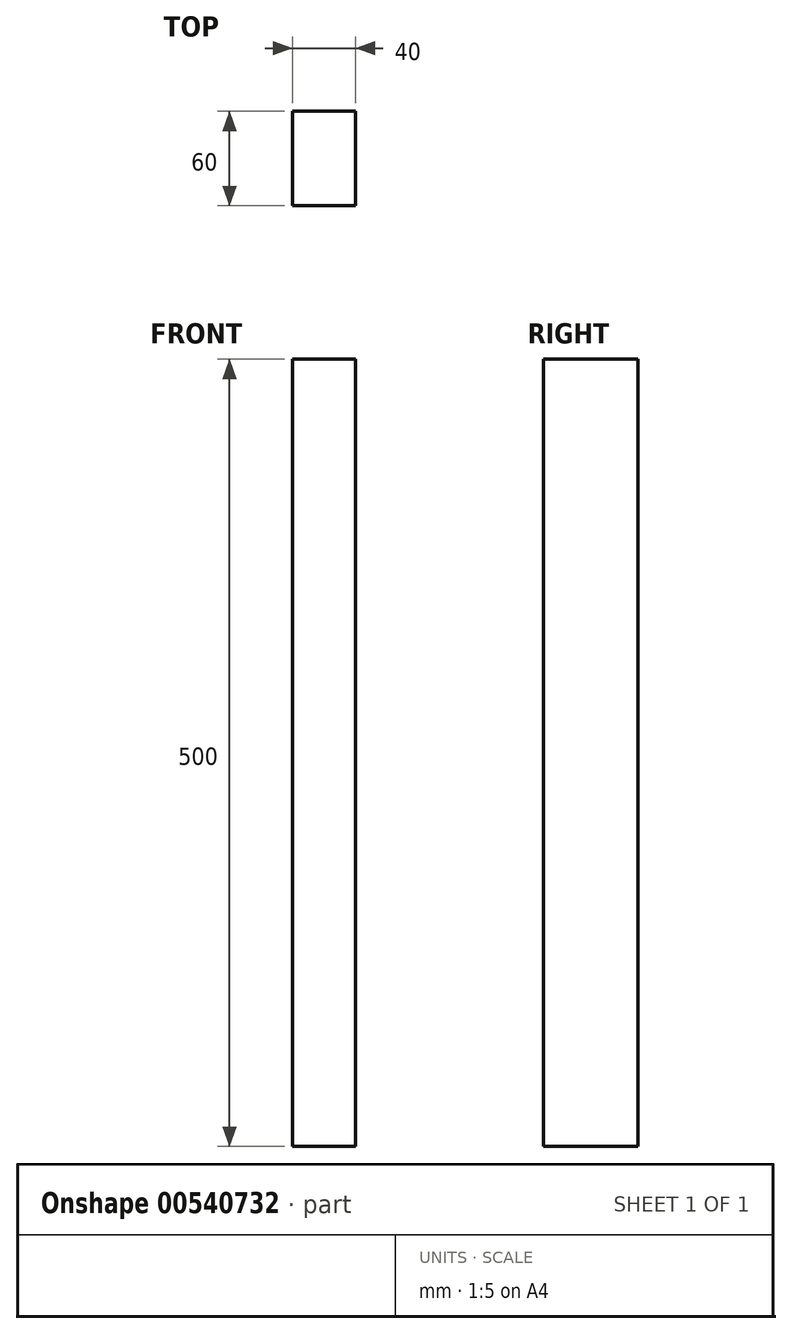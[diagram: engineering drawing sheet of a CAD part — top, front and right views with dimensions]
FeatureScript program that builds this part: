
annotation { "Feature Type Name" : "Feature", "Feature Type Description" : "" }
export const myFeature = defineFeature(function(context is Context, id is Id, definition is map)
    precondition{}
    {
        {
            var Q0;
            Q0=qCreatedBy(makeId("Top.planeOp"),FACE);
            var sketch = newSketch(context, id + "F0", { "sketchPlane" : qUnion([Q0])});
            skLineSegment(sketch, "E0.bottom", {"start": v(0, 0) * mm, "end": v(40, 0) * mm});
            skLineSegment(sketch, "E0.top", {"start": v(0, -60) * mm, "end": v(40, -60) * mm});
            skLineSegment(sketch, "E0.left", {"start": v(0, 0) * mm, "end": v(0, -60) * mm});
            skLineSegment(sketch, "E0.right", {"start": v(40, 0) * mm, "end": v(40, -60) * mm});
            skSolve(sketch);
        }
        {
            var Q0;
            Q0=makeQuery(id+"F0.imprint","IMPRINT",FACE,{"disambiguationData":[TD([[makeQuery(id+"F0.imprint","IMPRINT",EDGE,{"derivedFrom":sQuery(id+"F0.wireOp",EDGE,"E0.bottom")}),-1.0]])]});
            extrude(context, id + "F1", {"entities" : qUnion([Q0]), "depth" : 500 * mm, "offsetDistance" : 25 * mm});
        }
    });
